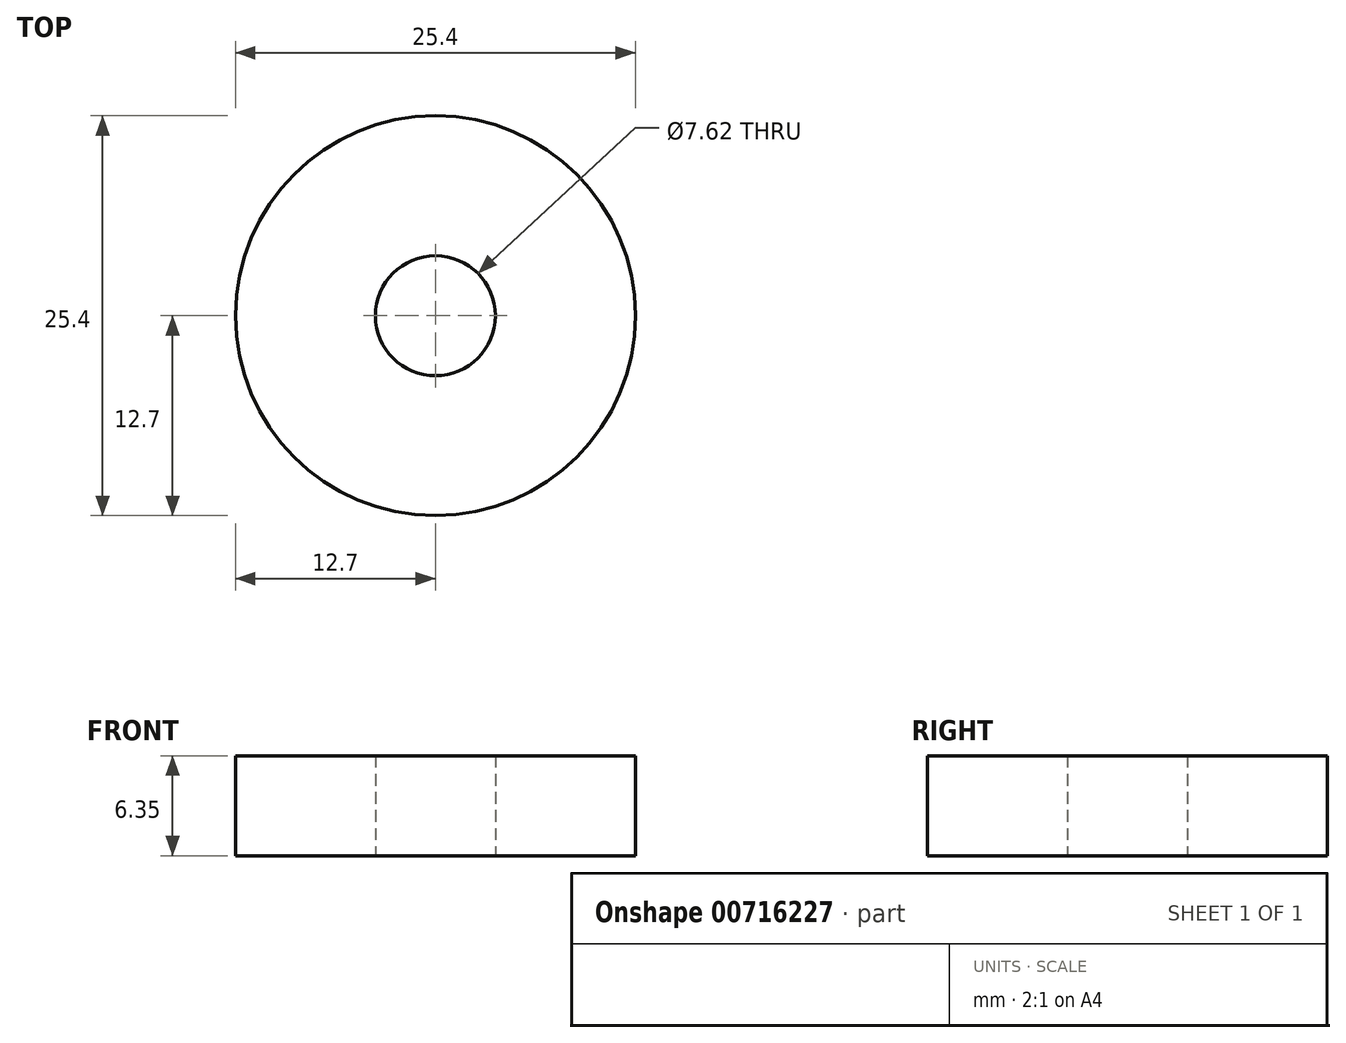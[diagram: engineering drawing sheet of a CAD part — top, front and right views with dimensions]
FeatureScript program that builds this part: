
annotation { "Feature Type Name" : "Feature", "Feature Type Description" : "" }
export const myFeature = defineFeature(function(context is Context, id is Id, definition is map)
    precondition{}
    {
        {
            var Q0;
            Q0=qCreatedBy(makeId("Top.planeOp"),FACE);
            var sketch = newSketch(context, id + "F0", { "sketchPlane" : qUnion([Q0])});
            skCircle(sketch, "E0", {"center": v(0, 0) * mm, "radius": 12.7 * mm});
            skCircle(sketch, "E1", {"center": v(0, 0) * mm, "radius": 3.81 * mm});
            skSolve(sketch);
        }
        {
            var Q0;
            Q0=makeQuery(id+"F0.imprint","IMPRINT",FACE,{"disambiguationData":[TD([[makeQuery(id+"F0.imprint","IMPRINT",EDGE,{"derivedFrom":sQuery(id+"F0.wireOp",EDGE,"E0")}),1.0]])]});
            extrude(context, id + "F1", {"entities" : qUnion([Q0]), "depth" : 6.35 * mm, "offsetDistance" : 25.4 * mm});
        }
    });
